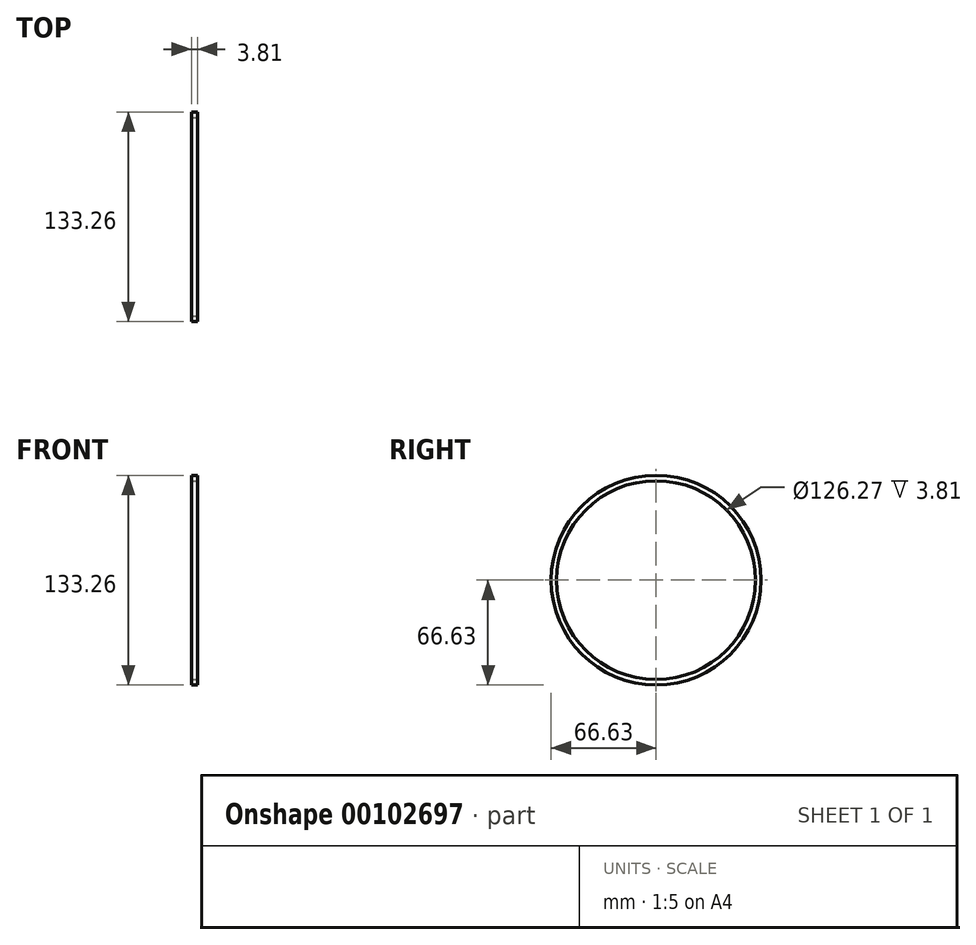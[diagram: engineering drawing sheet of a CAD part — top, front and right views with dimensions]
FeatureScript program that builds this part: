
annotation { "Feature Type Name" : "Feature", "Feature Type Description" : "" }
export const myFeature = defineFeature(function(context is Context, id is Id, definition is map)
    precondition{}
    {
        {
            var Q0;
            Q0=qCreatedBy(makeId("Right.planeOp"),FACE);
            var sketch = newSketch(context, id + "F0", { "sketchPlane" : qUnion([Q0])});
            skCircle(sketch, "E0", {"center": v(0, 0) * mm, "radius": 66.63 * mm});
            skSolve(sketch);
        }
        {
            var Q0;
            Q0 = qSketchRegion(id + "F0", true);
            extrude(context, id + "F1", {"entities" : qUnion([Q0]), "depth" : 3.8 * mm});
        }
        {
            var Q0;
            Q0=makeQuery(id+"F1.opExtrude","CAP_FACE",FACE,{"disambiguationData":[OSD([sQuery(id+"F0.wireOp",EDGE,"E0")])],"isStart":false});
            var sketch = newSketch(context, id + "F2", { "sketchPlane" : qUnion([Q0])});
            skCircle(sketch, "E1", {"center": v(0, 0) * mm, "radius": 63.14 * mm});
            skSolve(sketch);
        }
        {
            var Q0;
            Q0 = qSketchRegion(id + "F2", true);
            extrude(context, id + "F3", {"entities" : qUnion([Q0]), "operationType" : NewBodyOperationType.REMOVE, "endBound" : BoundingType.THROUGH_ALL, "oppositeDirection" : true, "depth" : 25.4 * mm});
        }
    });
